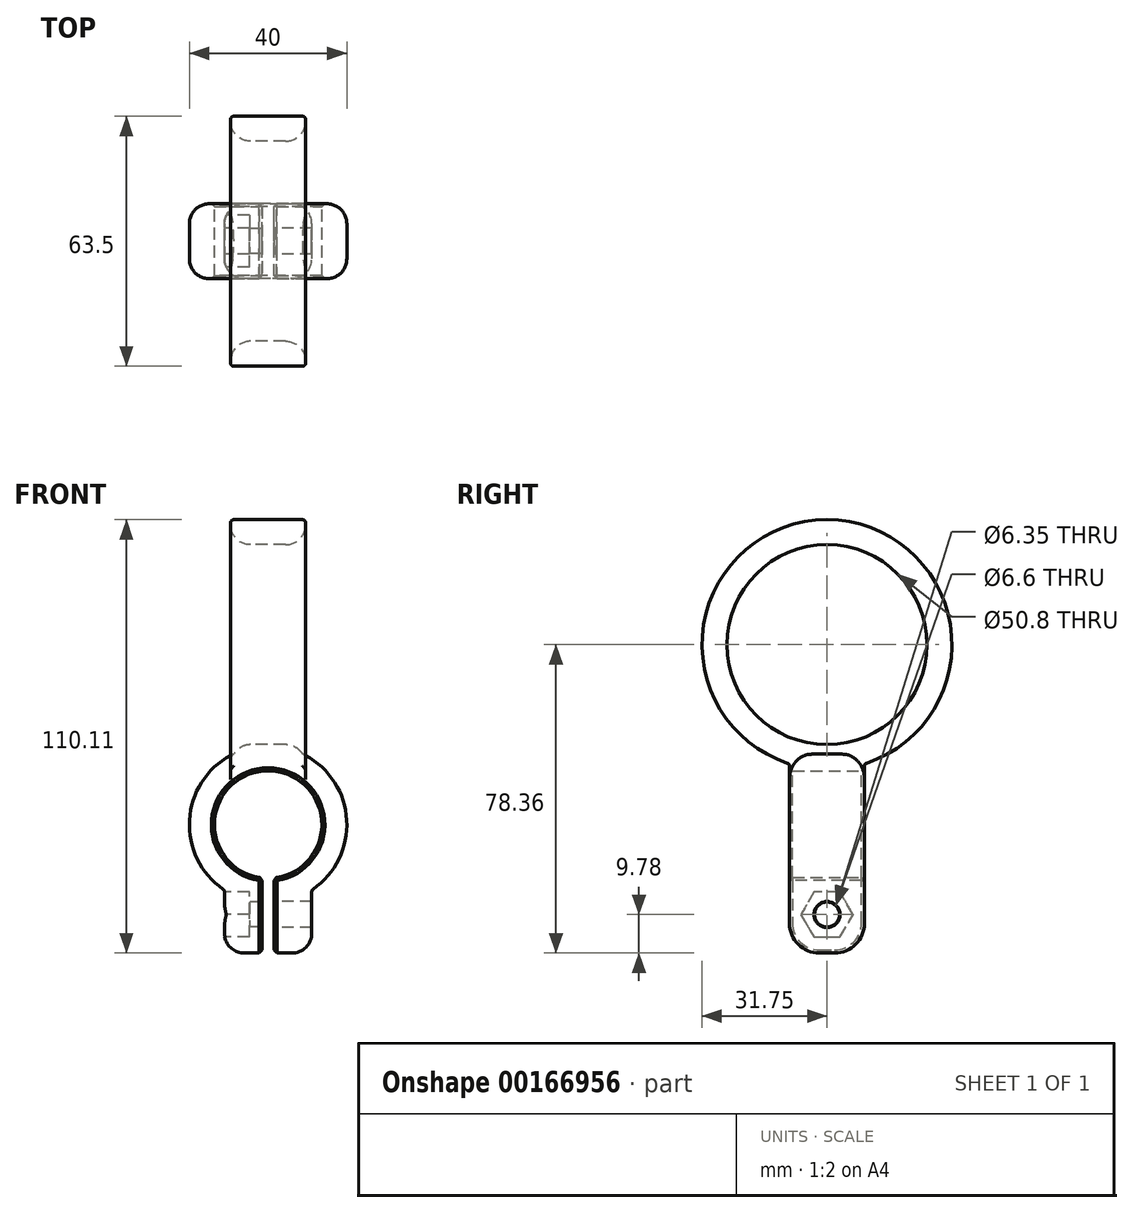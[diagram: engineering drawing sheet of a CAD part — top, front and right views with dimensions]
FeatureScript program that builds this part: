
annotation { "Feature Type Name" : "Feature", "Feature Type Description" : "" }
export const myFeature = defineFeature(function(context is Context, id is Id, definition is map)
    precondition{}
    {
        {
            var Q0;
            Q0=qCreatedBy(makeId("Front.planeOp"),FACE);
            var sketch = newSketch(context, id + "F0", { "sketchPlane" : qUnion([Q0])});
            skArc(sketch, "E0", {"start": v(1.57, -13.56) * mm, "mid": v(0, 13.65) * mm, "end": v(-1.57, -13.56) * mm});
            skArc(sketch, "E1.0", {"start": v(11.1, -16.64) * mm, "mid": v(0, 20) * mm, "end": v(-11.1, -16.64) * mm});
            skLineSegment(sketch, "E2", {"start": v(-1.57, -13.56) * mm, "end": v(-1.57, -19.94) * mm});
            skLineSegment(sketch, "E3.MirrorCS", {"start": v(1.57, -13.56) * mm, "end": v(1.57, -19.94) * mm});
            skLineSegment(sketch, "E4", {"start": v(-1.57, -19.94) * mm, "end": v(-1.57, -32.64) * mm});
            skLineSegment(sketch, "E5", {"start": v(-1.57, -32.64) * mm, "end": v(-11.1, -32.64) * mm});
            skLineSegment(sketch, "E6", {"start": v(-11.1, -32.64) * mm, "end": v(-11.1, -16.64) * mm});
            skLineSegment(sketch, "E7.MirrorCS", {"start": v(1.57, -19.94) * mm, "end": v(1.57, -32.64) * mm});
            skLineSegment(sketch, "E8.MirrorCS", {"start": v(1.57, -32.64) * mm, "end": v(11.1, -32.64) * mm});
            skLineSegment(sketch, "E9.MirrorCS", {"start": v(11.1, -32.64) * mm, "end": v(11.1, -16.64) * mm});
            skSolve(sketch);
        }
        {
            var Q0;
            Q0=makeQuery(id+"F0.imprint","IMPRINT",FACE,{"disambiguationData":[TD([[makeQuery(id+"F0.imprint","IMPRINT",EDGE,{"derivedFrom":sQuery(id+"F0.wireOp",EDGE,"E0")}),-1.0]])]});
            extrude(context, id + "F1", {"entities" : qUnion([Q0]), "endBound" : BoundingType.SYMMETRIC, "depth" : 19.05 * mm});
        }
        {
            var Q0;
            Q0=makeQuery(id+"F1.opExtrude","CAP_EDGE",EDGE,{"disambiguationData":[OSD([sQuery(id+"F0.wireOp",EDGE,"E8.MirrorCS")])],"isStart":true});
            var Q1;
            Q1=makeQuery(id+"F1.opExtrude","CAP_EDGE",EDGE,{"disambiguationData":[OSD([sQuery(id+"F0.wireOp",EDGE,"E5")])],"isStart":true});
            var Q2;
            Q2=makeQuery(id+"F1.opExtrude","CAP_EDGE",EDGE,{"disambiguationData":[OSD([sQuery(id+"F0.wireOp",EDGE,"E8.MirrorCS")])],"isStart":false});
            var Q3;
            Q3=makeQuery(id+"F1.opExtrude","CAP_EDGE",EDGE,{"disambiguationData":[OSD([sQuery(id+"F0.wireOp",EDGE,"E5")])],"isStart":false});
            fillet(context, id + "F2", {"entities" : qUnion([Q0, Q1, Q2, Q3]), "radius" : 7.62 * mm, "tangentPropagation" : true, "allowEdgeOverflow" : false});
        }
        {
            var Q0;
            Q0=makeQuery(id+"F1.opExtrude","CAP_EDGE",EDGE,{"disambiguationData":[OSD([sQuery(id+"F0.wireOp",EDGE,"E0")])],"isStart":false});
            var Q1;
            Q1=makeQuery(id+"F1.opExtrude","CAP_EDGE",EDGE,{"disambiguationData":[OSD([sQuery(id+"F0.wireOp",EDGE,"E0")])],"isStart":true});
            var Q2;
            Q2=makeQuery(id+"F1.opExtrude","CAP_EDGE",EDGE,{"disambiguationData":[OSD([sQuery(id+"F0.wireOp",EDGE,"E2"),sQuery(id+"F0.wireOp",EDGE,"E4")])],"isStart":false});
            var Q3;
            Q3=makeQuery(id+"F1.opExtrude","CAP_EDGE",EDGE,{"disambiguationData":[OSD([sQuery(id+"F0.wireOp",EDGE,"E3.MirrorCS"),sQuery(id+"F0.wireOp",EDGE,"E7.MirrorCS")])],"isStart":false});
            var Q4;
            Q4=makeQuery(id+"F1.opExtrude","CAP_EDGE",EDGE,{"disambiguationData":[OSD([sQuery(id+"F0.wireOp",EDGE,"E3.MirrorCS"),sQuery(id+"F0.wireOp",EDGE,"E7.MirrorCS")])],"isStart":true});
            var Q5;
            Q5=makeQuery(id+"F1.opExtrude","CAP_EDGE",EDGE,{"disambiguationData":[OSD([sQuery(id+"F0.wireOp",EDGE,"E2"),sQuery(id+"F0.wireOp",EDGE,"E4")])],"isStart":true});
            var Q6;
            Q6=makeQuery(id+"F1.opExtrude","SWEPT_EDGE",EDGE,{"disambiguationData":[OSD([sQuery(id+"F0.wireOp",EDGE,"E0"),sQuery(id+"F0.wireOp",EDGE,"E2")])]});
            var Q7;
            Q7=makeQuery(id+"F1.opExtrude","SWEPT_EDGE",EDGE,{"disambiguationData":[OSD([sQuery(id+"F0.wireOp",EDGE,"E0"),sQuery(id+"F0.wireOp",EDGE,"E3.MirrorCS")])]});
            var Q8;
            Q8=makeQuery(id+"F1.opExtrude","SWEPT_EDGE",EDGE,{"disambiguationData":[OSD([sQuery(id+"F0.wireOp",EDGE,"E7.MirrorCS"),sQuery(id+"F0.wireOp",EDGE,"E8.MirrorCS")])]});
            var Q9;
            Q9=makeQuery(id+"F1.opExtrude","SWEPT_EDGE",EDGE,{"disambiguationData":[OSD([sQuery(id+"F0.wireOp",EDGE,"E4"),sQuery(id+"F0.wireOp",EDGE,"E5")])]});
            chamfer(context, id + "F3", {"entities" : qUnion([Q0, Q1, Q2, Q3, Q4, Q5, Q6, Q7, Q8, Q9]), "width" : 0.76 * mm, "tangentPropagation" : true});
        }
        {
            var Q0;
            Q0=makeQuery(id+"F1.opExtrude","SWEPT_EDGE",EDGE,{"disambiguationData":[OSD([sQuery(id+"F0.wireOp",EDGE,"E1.0"),sQuery(id+"F0.wireOp",EDGE,"E9.MirrorCS")])]});
            var Q1;
            Q1=makeQuery(id+"F1.opExtrude","SWEPT_EDGE",EDGE,{"disambiguationData":[OSD([sQuery(id+"F0.wireOp",EDGE,"E1.0"),sQuery(id+"F0.wireOp",EDGE,"E6")])]});
            fillet(context, id + "F4", {"entities" : qUnion([Q0, Q1]), "radius" : 0.79 * mm, "tangentPropagation" : true, "allowEdgeOverflow" : false});
        }
        {
            var Q0;
            Q0=makeQuery(id+"F1.opExtrude","SWEPT_FACE",FACE,{"disambiguationData":[OSD([sQuery(id+"F0.wireOp",EDGE,"E6")])]});
            var sketch = newSketch(context, id + "F5", { "sketchPlane" : qUnion([Q0])});
            skCircle(sketch, "E10", {"center": v(0, -22.86) * mm, "radius": 3.18 * mm});
            skSolve(sketch);
        }
        {
            var Q0;
            Q0=makeQuery(id+"F5.imprint","IMPRINT",FACE,{"disambiguationData":[TD([[makeQuery(id+"F5.imprint","IMPRINT",EDGE,{"derivedFrom":sQuery(id+"F5.wireOp",EDGE,"E10")}),1.0]])]});
            extrude(context, id + "F6", {"entities" : qUnion([Q0]), "operationType" : NewBodyOperationType.REMOVE, "endBound" : BoundingType.UP_TO_NEXT, "oppositeDirection" : true, "depth" : 25.4 * mm});
        }
        {
            var Q0;
            Q0=makeQuery(id+"F1.opExtrude","SWEPT_FACE",FACE,{"disambiguationData":[OSD([sQuery(id+"F0.wireOp",EDGE,"E3.MirrorCS"),sQuery(id+"F0.wireOp",EDGE,"E7.MirrorCS")])]});
            var sketch = newSketch(context, id + "F7", { "sketchPlane" : qUnion([Q0])});
            skCircle(sketch, "E11.0", {"center": v(0, -22.86) * mm, "radius": 3.18 * mm});
            skCircle(sketch, "E12", {"center": v(0, -22.86) * mm, "radius": 3.3 * mm});
            skSolve(sketch);
        }
        {
            var Q0;
            Q0=makeQuery(id+"F7.imprint","IMPRINT",FACE,{"disambiguationData":[TD([[makeQuery(id+"F7.imprint","IMPRINT",EDGE,{"derivedFrom":sQuery(id+"F7.wireOp",EDGE,"E11.0")}),1.0]])]});
            var Q1;
            Q1=makeQuery(id+"F7.imprint","IMPRINT",FACE,{"disambiguationData":[TD([[makeQuery(id+"F7.imprint","IMPRINT",EDGE,{"derivedFrom":sQuery(id+"F7.wireOp",EDGE,"E11.0")}),-1.0]])]});
            extrude(context, id + "F8", {"entities" : qUnion([Q0, Q1]), "operationType" : NewBodyOperationType.REMOVE, "endBound" : BoundingType.UP_TO_NEXT, "oppositeDirection" : true, "depth" : 25.4 * mm});
        }
        {
            var Q0;
            Q0=qCreatedBy(makeId("Right.planeOp"),FACE);
            var sketch = newSketch(context, id + "F9", { "sketchPlane" : qUnion([Q0])});
            skCircle(sketch, "E13", {"center": v(0, 45.72) * mm, "radius": 25.4 * mm});
            skCircle(sketch, "E14.0", {"center": v(0, 45.72) * mm, "radius": 31.75 * mm});
            skSolve(sketch);
        }
        {
            var Q0;
            Q0=makeQuery(id+"F9.imprint","IMPRINT",FACE,{"disambiguationData":[TD([[makeQuery(id+"F9.imprint","IMPRINT",EDGE,{"derivedFrom":sQuery(id+"F9.wireOp",EDGE,"E13")}),-1.0]])]});
            extrude(context, id + "F10", {"entities" : qUnion([Q0]), "operationType" : NewBodyOperationType.ADD, "endBound" : BoundingType.SYMMETRIC, "depth" : 19.05 * mm});
        }
        {
            var Q0;
            Q0=makeQuery(id+"F10.opExtrude","CAP_EDGE",EDGE,{"disambiguationData":[OSD([sQuery(id+"F9.wireOp",EDGE,"E13")])],"isStart":false});
            var Q1;
            Q1=makeQuery(id+"F10.opExtrude","CAP_EDGE",EDGE,{"disambiguationData":[OSD([sQuery(id+"F9.wireOp",EDGE,"E13")])],"isStart":true});
            fillet(context, id + "F11", {"entities" : qUnion([Q0, Q1]), "radius" : 5.08 * mm, "tangentPropagation" : true, "allowEdgeOverflow" : false});
        }
        {
            var Q0;
            {var subQ0=sQuery(id+"F0.wireOp",EDGE,"E6");var subQ1=sQuery(id+"F0.wireOp",EDGE,"E1.0");Q0=makeQuery(id+"F10.boolean.opBoolean","SPLIT",EDGE,{"disambiguationData":[TD([makeQuery(id+"F4.opFillet","BLEND_FACE",FACE,{"disambiguationData":[OSD([subQ1,subQ0])]})])],"derivedFrom":makeQuery(id+"F1.opExtrude","CAP_EDGE",EDGE,{"disambiguationData":[OSD([subQ1])],"isStart":false})});}
            var Q1;
            {var subQ0=sQuery(id+"F0.wireOp",EDGE,"E9.MirrorCS");var subQ1=sQuery(id+"F0.wireOp",EDGE,"E1.0");Q1=makeQuery(id+"F10.boolean.opBoolean","SPLIT",EDGE,{"disambiguationData":[TD([makeQuery(id+"F4.opFillet","BLEND_FACE",FACE,{"disambiguationData":[OSD([subQ1,subQ0])]})])],"derivedFrom":makeQuery(id+"F1.opExtrude","CAP_EDGE",EDGE,{"disambiguationData":[OSD([subQ1])],"isStart":false})});}
            fillet(context, id + "F12", {"entities" : qUnion([Q0, Q1]), "radius" : 5.08 * mm, "tangentPropagation" : true, "allowEdgeOverflow" : false});
        }
        {
            var Q0;
            Q0=makeQuery(id+"F10.opExtrude","CAP_EDGE",EDGE,{"disambiguationData":[OSD([sQuery(id+"F9.wireOp",EDGE,"E14.0")])],"isStart":true});
            var Q1;
            Q1=makeQuery(id+"F10.opExtrude","CAP_EDGE",EDGE,{"disambiguationData":[OSD([sQuery(id+"F9.wireOp",EDGE,"E14.0")])],"isStart":false});
            var Q2;
            Q2=makeQuery(id+"F10.boolean.opBoolean","INTERSECT",EDGE,{"derivedFrom":[makeQuery(id+"F1.opExtrude","CAP_FACE",FACE,{"disambiguationData":[OSD([sQuery(id+"F0.wireOp",EDGE,"E0"),sQuery(id+"F0.wireOp",EDGE,"E1.0"),sQuery(id+"F0.wireOp",EDGE,"E2"),sQuery(id+"F0.wireOp",EDGE,"E3.MirrorCS"),sQuery(id+"F0.wireOp",EDGE,"E4"),sQuery(id+"F0.wireOp",EDGE,"E5"),sQuery(id+"F0.wireOp",EDGE,"E6"),sQuery(id+"F0.wireOp",EDGE,"E7.MirrorCS"),sQuery(id+"F0.wireOp",EDGE,"E8.MirrorCS"),sQuery(id+"F0.wireOp",EDGE,"E9.MirrorCS")])],"isStart":false}),makeQuery(id+"F10.opExtrude","SWEPT_FACE",FACE,{"disambiguationData":[OSD([sQuery(id+"F9.wireOp",EDGE,"E14.0")])]})]});
            var Q3;
            Q3=makeQuery(id+"F10.boolean.opBoolean","INTERSECT",EDGE,{"derivedFrom":[makeQuery(id+"F1.opExtrude","CAP_FACE",FACE,{"disambiguationData":[OSD([sQuery(id+"F0.wireOp",EDGE,"E0"),sQuery(id+"F0.wireOp",EDGE,"E1.0"),sQuery(id+"F0.wireOp",EDGE,"E2"),sQuery(id+"F0.wireOp",EDGE,"E3.MirrorCS"),sQuery(id+"F0.wireOp",EDGE,"E4"),sQuery(id+"F0.wireOp",EDGE,"E5"),sQuery(id+"F0.wireOp",EDGE,"E6"),sQuery(id+"F0.wireOp",EDGE,"E7.MirrorCS"),sQuery(id+"F0.wireOp",EDGE,"E8.MirrorCS"),sQuery(id+"F0.wireOp",EDGE,"E9.MirrorCS")])],"isStart":true}),makeQuery(id+"F10.opExtrude","SWEPT_FACE",FACE,{"disambiguationData":[OSD([sQuery(id+"F9.wireOp",EDGE,"E14.0")])]})]});
            fillet(context, id + "F13", {"entities" : qUnion([Q0, Q1, Q2, Q3]), "radius" : 0.76 * mm, "tangentPropagation" : true, "allowEdgeOverflow" : false});
        }
        {
            var Q0;
            Q0=makeQuery(id+"F1.opExtrude","SWEPT_FACE",FACE,{"disambiguationData":[OSD([sQuery(id+"F0.wireOp",EDGE,"E6")])]});
            var sketch = newSketch(context, id + "F14", { "sketchPlane" : qUnion([Q0])});
            skCircle(sketch, "E15.cCircle", {"center": v(0, -22.86) * mm, "radius": 5.72 * mm, "construction": true});
            skLineSegment(sketch, "E15.0", {"start": v(3.3, -28.58) * mm, "end": v(-3.3, -28.58) * mm});
            skLineSegment(sketch, "E15.1", {"start": v(-3.3, -28.58) * mm, "end": v(-6.6, -22.86) * mm});
            skLineSegment(sketch, "E15.2", {"start": v(-6.6, -22.86) * mm, "end": v(-3.3, -17.14) * mm});
            skLineSegment(sketch, "E15.3", {"start": v(-3.3, -17.15) * mm, "end": v(3.3, -17.14) * mm});
            skLineSegment(sketch, "E15.4", {"start": v(3.3, -17.14) * mm, "end": v(6.6, -22.86) * mm});
            skLineSegment(sketch, "E15.5", {"start": v(6.6, -22.86) * mm, "end": v(3.3, -28.58) * mm});
            skPoint(sketch, "E15.0.midPoint", {"position": v(0, -28.58) * mm});
            skSolve(sketch);
        }
        {
            var Q0;
            {var subQ0=sQuery(id+"F14.wireOp",EDGE,"E15.3");Q0=makeQuery(id+"F14.imprint","IMPRINT",FACE,{"disambiguationData":[TD([[makeQuery(id+"F14.imprint","IMPRINT",EDGE,{"derivedFrom":subQ0}),-1.0]])]});}
            var Q1;
            Q1=makeQuery(id+"F14.imprint","IMPRINT",FACE,{"disambiguationData":[TD([[makeQuery(id+"F14.imprint","IMPRINT",EDGE,{"derivedFrom":sQuery(id+"F14.wireOp",EDGE,"E15.0")}),-1.0]])]});
            extrude(context, id + "F15", {"entities" : qUnion([Q0, Q1]), "operationType" : NewBodyOperationType.REMOVE, "oppositeDirection" : true, "depth" : 6.35 * mm});
        }
    });
